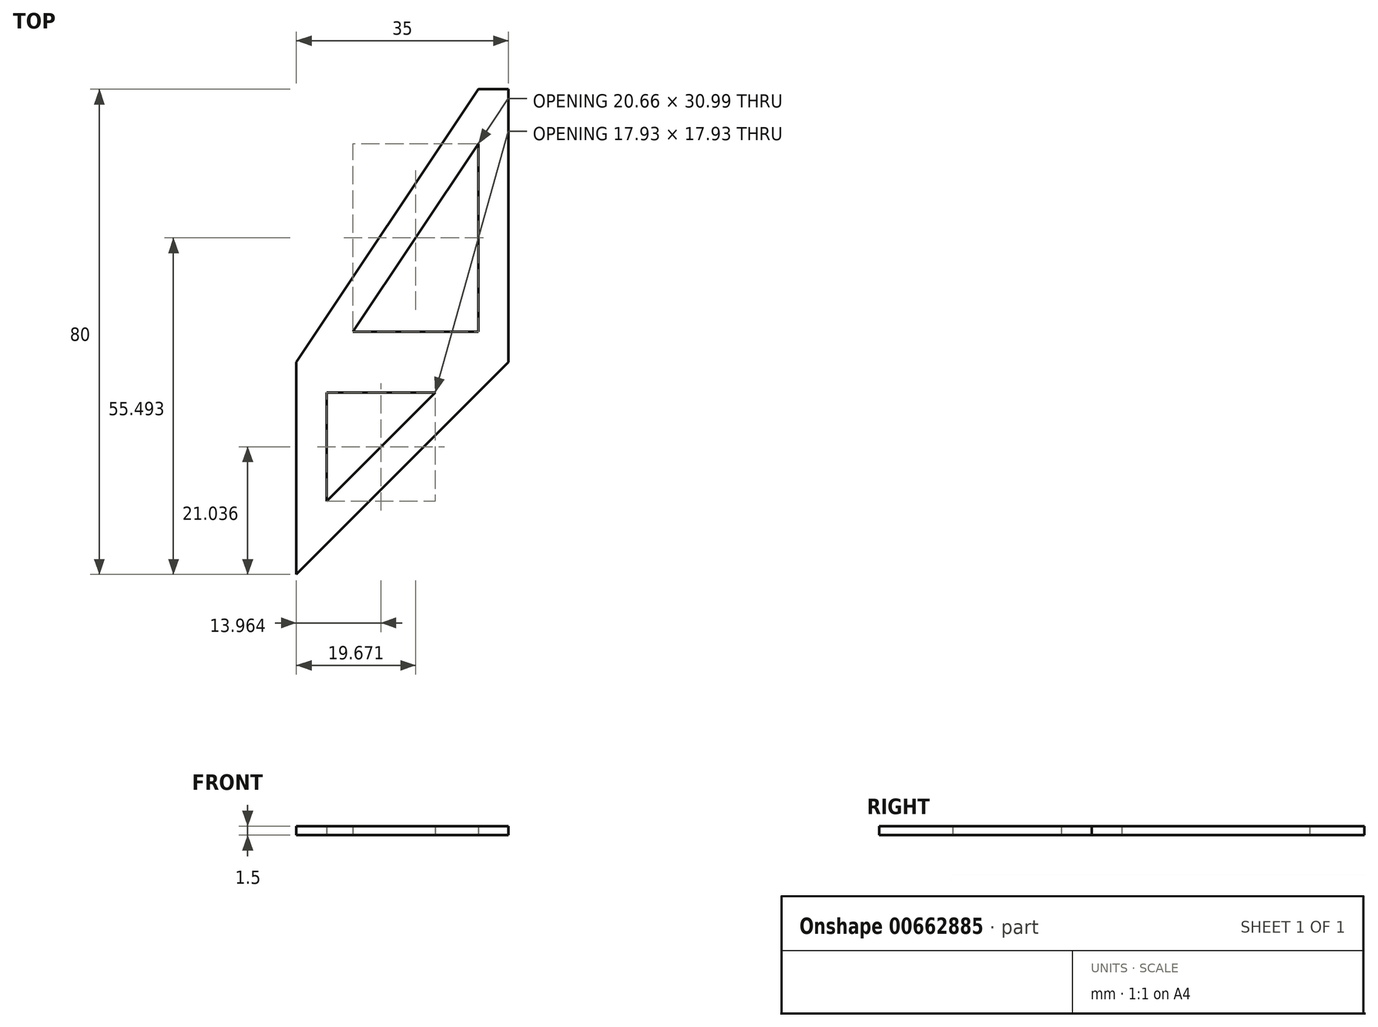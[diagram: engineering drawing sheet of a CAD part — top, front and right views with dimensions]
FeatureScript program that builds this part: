
annotation { "Feature Type Name" : "Feature", "Feature Type Description" : "" }
export const myFeature = defineFeature(function(context is Context, id is Id, definition is map)
    precondition{}
    {
        {
            var Q0;
            Q0=qCreatedBy(makeId("Top.planeOp"),FACE);
            var sketch = newSketch(context, id + "F0", { "sketchPlane" : qUnion([Q0])});
            skLineSegment(sketch, "E0", {"start": v(0, 0) * mm, "end": v(35, 0) * mm});
            skLineSegment(sketch, "E1", {"start": v(35, 0) * mm, "end": v(35, 45) * mm});
            skLineSegment(sketch, "E2", {"start": v(35, 45) * mm, "end": v(30, 45) * mm});
            skLineSegment(sketch, "E3", {"start": v(30, 45) * mm, "end": v(0, 0) * mm});
            skLineSegment(sketch, "E4", {"start": v(0, -35) * mm, "end": v(35, 0) * mm});
            skLineSegment(sketch, "E5", {"start": v(0, 0) * mm, "end": v(0, -35) * mm});
            skLineSegment(sketch, "E6.0", {"start": v(30, 35.99) * mm, "end": v(9.34, 5) * mm});
            skLineSegment(sketch, "E6.1", {"start": v(30, 5) * mm, "end": v(30, 35.99) * mm});
            skLineSegment(sketch, "E6.2", {"start": v(9.34, 5) * mm, "end": v(30, 5) * mm});
            skLineSegment(sketch, "E7.0", {"start": v(5, -5) * mm, "end": v(5, -22.93) * mm});
            skLineSegment(sketch, "E7.1", {"start": v(5, -5) * mm, "end": v(22.93, -5) * mm});
            skLineSegment(sketch, "E7.2", {"start": v(5, -22.93) * mm, "end": v(22.93, -5) * mm});
            skLineSegment(sketch, "E8", {"start": v(0, -35) * mm, "end": v(121.03, -35) * mm, "construction": true});
            skSolve(sketch);
        }
        {
            var Q0;
            Q0 = qSketchRegion(id + "F0", true);
            extrude(context, id + "F1", {"entities" : qUnion([Q0]), "depth" : 1.5 * mm, "offsetDistance" : 25 * mm});
        }
    });
